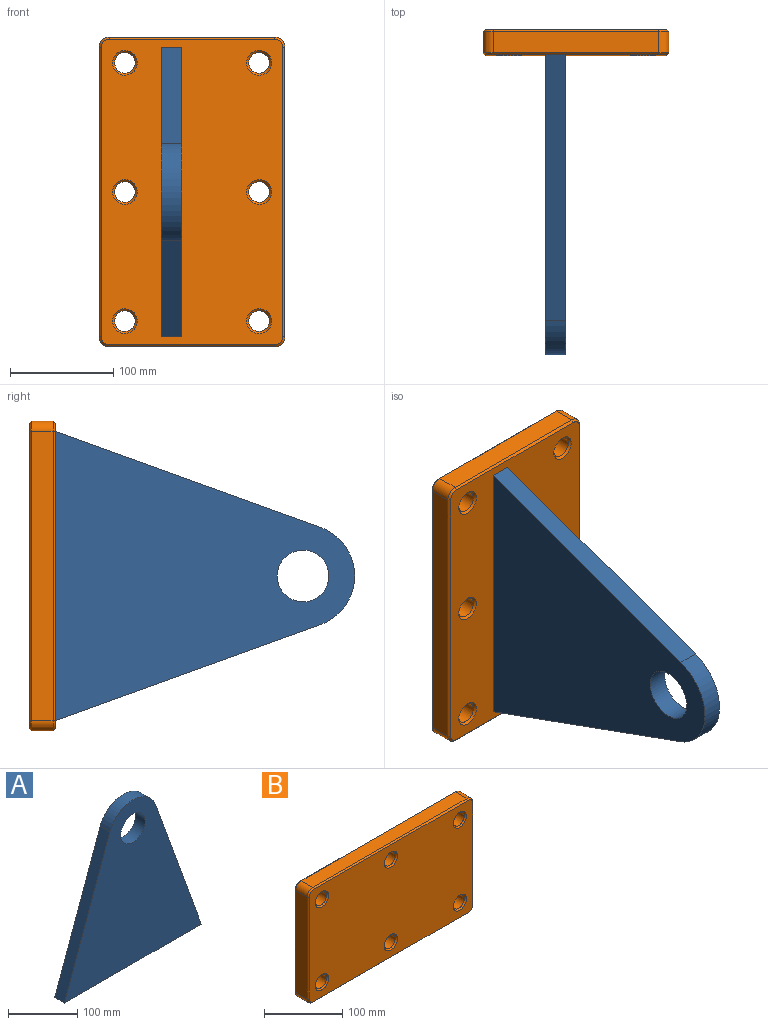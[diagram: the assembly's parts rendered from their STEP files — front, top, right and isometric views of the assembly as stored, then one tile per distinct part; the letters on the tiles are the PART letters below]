
ASSEMBLY  parts=2 mates=2
PART A: 7 faces, bbox 280x20x290 mm
  f0: plane 280x20mm, normal (0,0,-1), area 5600mm2, adj f1,f3,f5,f6
  f1: plane 257.01x92.98mm, normal (0.94,0,0.34), area 5466.3mm2, adj f0,f2,f5,f6
  f2: cylinder r=50mm len=94.04mm, axis (0,-1,0), area 2447.3mm2, adj f1,f3,f5,f6
  f3: plane 257.01x92.98mm, normal (-0.94,0,0.34), area 5466.3mm2, adj f0,f2,f5,f6
  f4: cylinder r=25mm len=50mm, axis (0,-1,0), area 3141.6mm2, adj f5,f6
  f5: plane 290x280mm, normal (0,1,0), area 48361.3mm2, adj f0,f1,f2,f3,f4
  f6: plane 290x280mm, normal (0,-1,0), area 48361.3mm2, adj f0,f1,f2,f3,f4
PART B: 44 faces, bbox 300x25x180 mm
  f0: plane 160x21mm, normal (1,0,0), area 3360mm2, adj f1,f13,f20,f28
  f1: cylinder r=10mm len=21mm, axis (0,-1,0), area 329.9mm2, adj f0,f2,f22,f30
  f2: plane 280x21mm, normal (0,0,1), area 5880mm2, adj f1,f3,f23,f31
  f3: cylinder r=10mm len=21mm, axis (0,-1,0), area 329.9mm2, adj f2,f4,f21,f29
  f4: plane 160x21mm, normal (-1,0,0), area 3360mm2, adj f3,f5,f19,f27
  f5: cylinder r=10mm len=21mm, axis (0,-1,0), area 329.9mm2, adj f4,f6,f17,f25
  f6: plane 280x21mm, normal (0,0,-1), area 5880mm2, adj f5,f13,f16,f24
  f7: cylinder r=10mm len=21mm, axis (0,-1,0), area 1319.5mm2, adj f35,f43
  f8: cylinder r=10mm len=21mm, axis (0,-1,0), area 1319.5mm2, adj f34,f38
  f9: cylinder r=10mm len=21mm, axis (0,-1,0), area 1319.5mm2, adj f36,f42
  f10: cylinder r=10mm len=21mm, axis (0,-1,0), area 1319.5mm2, adj f33,f39
  f11: cylinder r=10mm len=21mm, axis (0,-1,0), area 1319.5mm2, adj f37,f41
  f12: cylinder r=10mm len=21mm, axis (0,-1,0), area 1319.5mm2, adj f32,f40
  f13: cylinder r=10mm len=21mm, axis (0,-1,0), area 329.9mm2, adj f0,f6,f18,f26
  f14: plane 296x176mm, normal (0,1,0), area 49326.7mm2, adj f16,f17,f18,f19,f20,f21,f22,f23
  f15: plane 296x176mm, normal (0,-1,0), area 49326.7mm2, adj f24,f25,f26,f27,f28,f29,f30,f31
  f16: plane 280x2mm, normal (0,0.71,-0.71), area 792mm2, adj f6,f14,f17,f18
  f17: cone r=10mm half-angle=45deg, axis (0,-1,0), area 40mm2, adj f5,f14,f16,f19
  f18: cone r=10mm half-angle=45deg, axis (0,-1,0), area 40mm2, adj f13,f14,f16,f20
  f19: plane 160x2mm, normal (-0.71,0.71,0), area 452.5mm2, adj f4,f14,f17,f21
  f20: plane 160x2mm, normal (0.71,0.71,0), area 452.5mm2, adj f0,f14,f18,f22
  f21: cone r=10mm half-angle=45deg, axis (0,-1,0), area 40mm2, adj f3,f14,f19,f23
  f22: cone r=10mm half-angle=45deg, axis (0,-1,0), area 40mm2, adj f1,f14,f20,f23
  f23: plane 280x2mm, normal (0,0.71,0.71), area 792mm2, adj f2,f14,f21,f22
  f24: plane 280x2mm, normal (0,-0.71,-0.71), area 792mm2, adj f6,f15,f25,f26
  f25: cone r=8mm half-angle=45deg, axis (0,1,0), area 40mm2, adj f5,f15,f24,f27
  f26: cone r=8mm half-angle=45deg, axis (0,1,0), area 40mm2, adj f13,f15,f24,f28
  f27: plane 160x2mm, normal (-0.71,-0.71,0), area 452.5mm2, adj f4,f15,f25,f29
  f28: plane 160x2mm, normal (0.71,-0.71,0), area 452.5mm2, adj f0,f15,f26,f30
  f29: cone r=8mm half-angle=45deg, axis (0,1,0), area 40mm2, adj f3,f15,f27,f31
  f30: cone r=8mm half-angle=45deg, axis (0,1,0), area 40mm2, adj f1,f15,f28,f31
  f31: plane 280x2mm, normal (0,-0.71,0.71), area 792mm2, adj f2,f15,f29,f30
  f32: cone r=12mm half-angle=45deg, axis (0,1,0), area 195.5mm2, adj f12,f14
  f33: cone r=12mm half-angle=45deg, axis (0,1,0), area 195.5mm2, adj f10,f14
  f34: cone r=12mm half-angle=45deg, axis (0,1,0), area 195.5mm2, adj f8,f14
  f35: cone r=12mm half-angle=45deg, axis (0,1,0), area 195.5mm2, adj f7,f14
  f36: cone r=12mm half-angle=45deg, axis (0,1,0), area 195.5mm2, adj f9,f14
  f37: cone r=12mm half-angle=45deg, axis (0,1,0), area 195.5mm2, adj f11,f14
  f38: cone r=10mm half-angle=45deg, axis (0,-1,0), area 195.5mm2, adj f8,f15
  f39: cone r=10mm half-angle=45deg, axis (0,-1,0), area 195.5mm2, adj f10,f15
  f40: cone r=10mm half-angle=45deg, axis (0,-1,0), area 195.5mm2, adj f12,f15
  f41: cone r=10mm half-angle=45deg, axis (0,-1,0), area 195.5mm2, adj f11,f15
  f42: cone r=10mm half-angle=45deg, axis (0,-1,0), area 195.5mm2, adj f9,f15
  f43: cone r=10mm half-angle=45deg, axis (0,-1,0), area 195.5mm2, adj f7,f15
PLACE A rot(axis=(0.58,0.58,-0.58),120deg) t=(-30,0,490)mm
PLACE B rot(axis=(0.71,0,-0.71),180deg) t=(90,25,150)mm
MATE fastened A.f0 <-> B.f14  axis (0,-1,0) through (-30,0,140)mm
MATE planar A.f0 <-> B.f14  axis (0,1,0) through (-20,0,0)mm
